AUTODESK INVENTOR PART (.ipt)
format: ipt  version: 2021.3 (Build 253353000, 353)  size: 186,880 bytes
history: imported  units: in
note: dims shown in document units (in); Inventor stores cm internally (conversion verified against a paired STEP export)
features: imported_body x1
ambient origin geometry x8: Origin, YZ Plane, XZ Plane, XY Plane, X Axis, Y Axis, Z Axis, Center Point
bodies: Solid1 (imported_parasolid), Body1 (imported_parasolid)
feature tree (1):
  imported_body  NMx_Import_Brep_tag  [imported B-rep: ~6 faces, bbox_mm=None]
